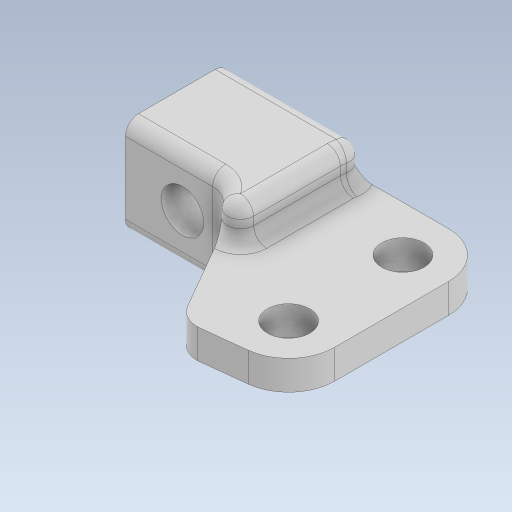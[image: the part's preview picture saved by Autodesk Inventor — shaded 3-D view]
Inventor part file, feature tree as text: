
AUTODESK INVENTOR PART (.ipt)
format: ipt  version: 2023 (Build 270158000, 158)  size: 503,296 bytes
history: native  units: in
note: dims shown in document units (in); Inventor stores cm internally (conversion verified against a paired STEP export)
features: extrude x3, fillet x3, sketch x2, plane x1, mirror x1, projected_geometry x1
ambient origin geometry x8: Origin, YZ Plane, XZ Plane, XY Plane, X Axis, Y Axis, Z Axis, Center Point
bodies: Solid1 (feature_tree)
feature tree (11):
  extrude  "Extrusion1"  Depth=0.2559in
  extrude  "Extrusion2"  Depth=0.1575in
  fillet  "Fillet1"  Radius=0.9843in
  fillet  "Fillet2"  Radius=0.4921in
  plane  "Work Plane1"
  mirror  "Mirror1"
  fillet  "Fillet3"  Radius=1.5748in
  extrude  "Extrusion4"  Depth=0.0787in
  sketch  "Sketch1"  dims[d0=0.689in d1=0.2559in]
  projected_geometry  "Projected Loop1"
  sketch  "Sketch4"  dims[d2=0.2559in d3=0.1575in d4=0.9843in d5=0.4921in d6=1.5748in d7=0.9843in d8=0.5906in d9=0.0in d10=0.1575in d11=120.0deg d12=0.2067in d13=0.0in d14=0.0787in d15=0.0787in d16=-0.0886in d20=0.0787in d21=0.5512in d22=0.5512in d23=0.2559in d24=0.0in d25=0.0in]
